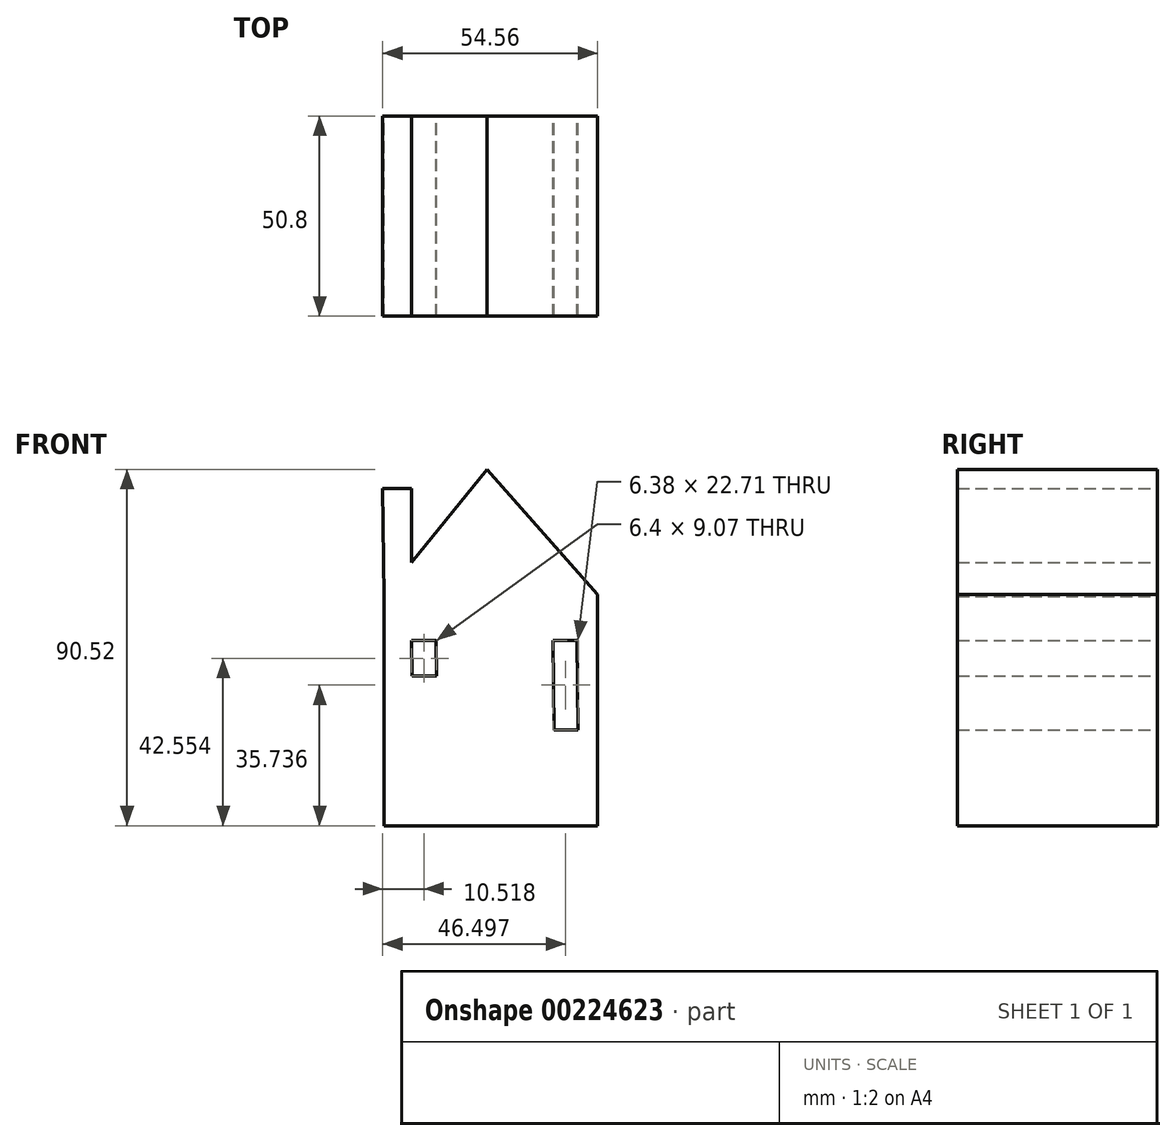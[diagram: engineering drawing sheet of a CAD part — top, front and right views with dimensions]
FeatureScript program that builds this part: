
annotation { "Feature Type Name" : "Feature", "Feature Type Description" : "" }
export const myFeature = defineFeature(function(context is Context, id is Id, definition is map)
    precondition{}
    {
        {
            var Q0;
            Q0=qCreatedBy(makeId("Front.planeOp"),FACE);
            var sketch = newSketch(context, id + "F0", { "sketchPlane" : qUnion([Q0])});
            skLineSegment(sketch, "E0", {"start": v(-30.02, 11.13) * mm, "end": v(-30.02, -47.1) * mm});
            skLineSegment(sketch, "E1", {"start": v(-31.24, -47.1) * mm, "end": v(24.23, -47.1) * mm});
            skLineSegment(sketch, "E2", {"start": v(24.23, -47.1) * mm, "end": v(24.23, 11.73) * mm});
            skLineSegment(sketch, "E3", {"start": v(24.23, 11.73) * mm, "end": v(-30.02, 11.13) * mm});
            skLineSegment(sketch, "E4", {"start": v(-30.02, 11.13) * mm, "end": v(-3.81, 43.43) * mm});
            skLineSegment(sketch, "E5", {"start": v(-3.81, 43.43) * mm, "end": v(24.23, 11.73) * mm});
            skLineSegment(sketch, "E6", {"start": v(-30.02, 11.13) * mm, "end": v(-30.33, 38.57) * mm});
            skLineSegment(sketch, "E7", {"start": v(-31.24, 38.56) * mm, "end": v(-23.01, 38.57) * mm});
            skLineSegment(sketch, "E8", {"start": v(-23.01, 38.57) * mm, "end": v(-23.01, 19.77) * mm});
            skLineSegment(sketch, "E9", {"start": v(-12.65, -47.1) * mm, "end": v(-12.65, -28.5) * mm});
            skLineSegment(sketch, "E10", {"start": v(-13.56, -28.5) * mm, "end": v(0, -28.35) * mm});
            skLineSegment(sketch, "E11", {"start": v(0, -28.35) * mm, "end": v(0.21, -47.1) * mm});
            skLineSegment(sketch, "E12", {"start": v(-23.01, 0) * mm, "end": v(-22.8, -18.14) * mm});
            skLineSegment(sketch, "E13", {"start": v(-22.1, -18.14) * mm, "end": v(-10.21, -18) * mm});
            skLineSegment(sketch, "E14", {"start": v(-10.21, -18) * mm, "end": v(-10.41, 0) * mm});
            skLineSegment(sketch, "E15", {"start": v(-10.41, 0) * mm, "end": v(-23.01, 0) * mm});
            skLineSegment(sketch, "E16", {"start": v(-16.71, 0) * mm, "end": v(-16.51, -18) * mm});
            skLineSegment(sketch, "E17", {"start": v(-22.91, -9.07) * mm, "end": v(-10.41, -9.07) * mm});
            skLineSegment(sketch, "E18", {"start": v(6.86, -2.29) * mm, "end": v(7.09, -22.7) * mm});
            skLineSegment(sketch, "E19", {"start": v(6.86, -22.7) * mm, "end": v(19.35, -22.7) * mm});
            skLineSegment(sketch, "E20", {"start": v(19.35, -22.7) * mm, "end": v(19.1, 0) * mm});
            skLineSegment(sketch, "E21", {"start": v(19.1, 0) * mm, "end": v(6.86, -0.14) * mm});
            skLineSegment(sketch, "E22", {"start": v(6.86, -0.14) * mm, "end": v(6.86, -2.29) * mm});
            skLineSegment(sketch, "E23", {"start": v(6.97, -9.07) * mm, "end": v(19.1, -9.07) * mm});
            skPoint(sketch, "E23.startSnap0", {"position": v(6.97, -12.5) * mm});
            skLineSegment(sketch, "E24", {"start": v(12.98, -0.07) * mm, "end": v(13.23, -22.7) * mm});
            skLineSegment(sketch, "E25", {"start": v(11.73, -22.1) * mm, "end": v(13.23, -22.7) * mm});
            skSolve(sketch);
        }
        {
            var Q0;
            Q0 = qSketchRegion(id + "F0", true);
            extrude(context, id + "F1", {"entities" : qUnion([Q0]), "depth" : 50.8 * mm});
        }
    });
